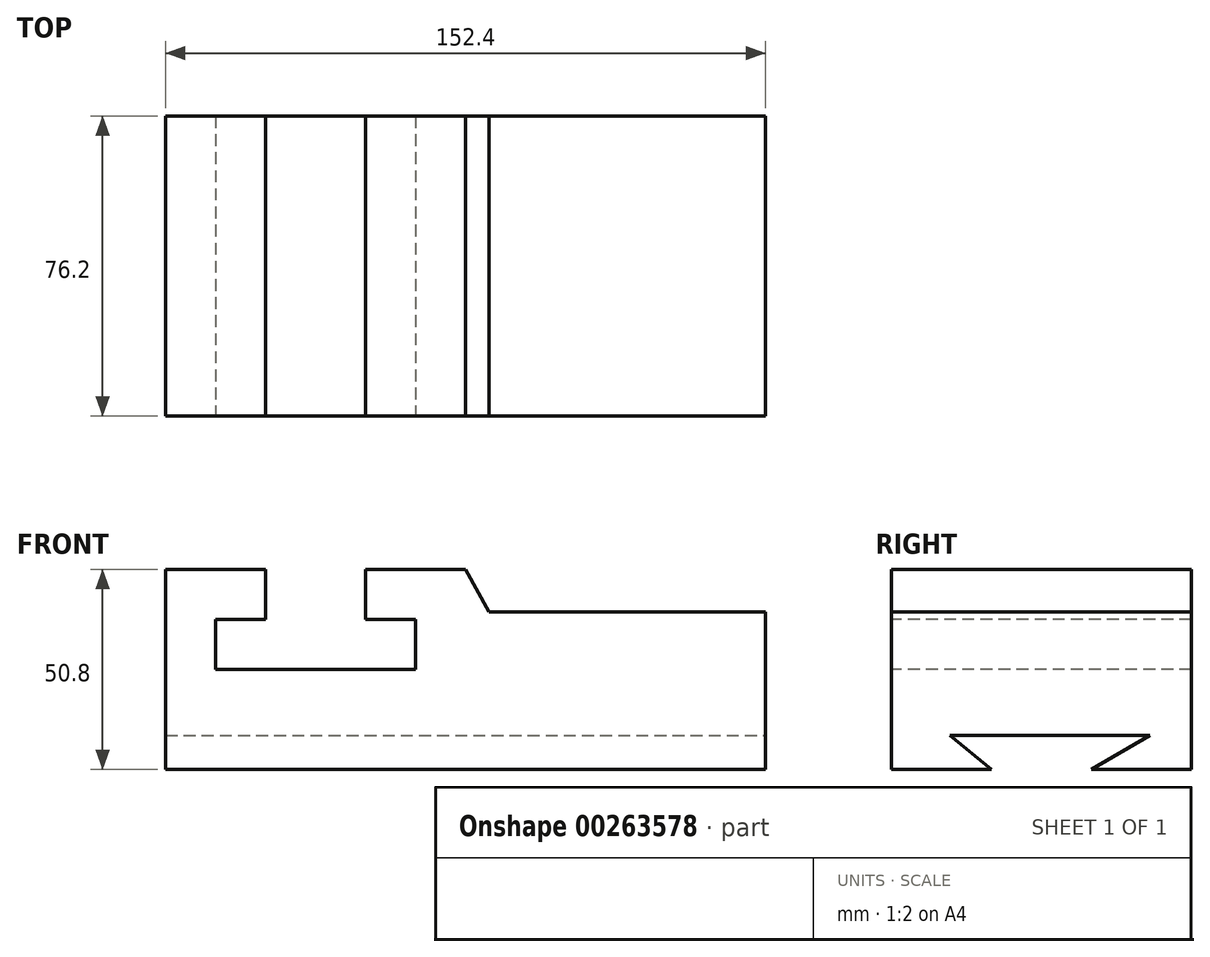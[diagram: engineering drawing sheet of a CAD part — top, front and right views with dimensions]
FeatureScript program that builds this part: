
annotation { "Feature Type Name" : "Feature", "Feature Type Description" : "" }
export const myFeature = defineFeature(function(context is Context, id is Id, definition is map)
    precondition{}
    {
        {
            var Q0;
            Q0=qCreatedBy(makeId("Front.planeOp"),FACE);
            var sketch = newSketch(context, id + "F0", { "sketchPlane" : qUnion([Q0])});
            skLineSegment(sketch, "E0.bottom", {"start": v(-122.18, 62.89) * mm, "end": v(30.22, 62.89) * mm});
            skLineSegment(sketch, "E0.top", {"start": v(-122.18, 12.09) * mm, "end": v(30.22, 12.09) * mm});
            skLineSegment(sketch, "E0.left", {"start": v(-122.18, 62.89) * mm, "end": v(-122.18, 12.09) * mm});
            skLineSegment(sketch, "E0.right", {"start": v(30.22, 62.89) * mm, "end": v(30.22, 12.09) * mm});
            skSolve(sketch);
        }
        {
            var Q0;
            Q0=makeQuery(id+"F0.imprint","IMPRINT",FACE,{"disambiguationData":[TD([[makeQuery(id+"F0.imprint","IMPRINT",EDGE,{"derivedFrom":sQuery(id+"F0.wireOp",EDGE,"E0.bottom")}),-1.0]])]});
            extrude(context, id + "F1", {"entities" : qUnion([Q0]), "depth" : 76.2 * mm});
        }
        {
            var Q0;
            Q0=makeQuery(id+"F1.opExtrude","CAP_FACE",FACE,{"disambiguationData":[OSD([sQuery(id+"F0.wireOp",EDGE,"E0.bottom"),sQuery(id+"F0.wireOp",EDGE,"E0.top"),sQuery(id+"F0.wireOp",EDGE,"E0.left"),sQuery(id+"F0.wireOp",EDGE,"E0.right")])],"isStart":false});
            var sketch = newSketch(context, id + "F2", { "sketchPlane" : qUnion([Q0])});
            skLineSegment(sketch, "E1", {"start": v(-96.78, 62.89) * mm, "end": v(-96.78, 50.19) * mm});
            skLineSegment(sketch, "E2", {"start": v(-96.78, 50.19) * mm, "end": v(-109.48, 50.19) * mm});
            skLineSegment(sketch, "E3", {"start": v(-109.48, 50.19) * mm, "end": v(-109.48, 37.49) * mm});
            skLineSegment(sketch, "E4", {"start": v(-109.48, 37.49) * mm, "end": v(-58.68, 37.49) * mm});
            skLineSegment(sketch, "E5", {"start": v(-58.68, 37.49) * mm, "end": v(-58.68, 50.19) * mm});
            skLineSegment(sketch, "E6", {"start": v(-58.68, 50.19) * mm, "end": v(-71.38, 50.19) * mm});
            skLineSegment(sketch, "E7", {"start": v(-71.38, 50.19) * mm, "end": v(-71.38, 62.89) * mm});
            skLineSegment(sketch, "E8", {"start": v(-71.38, 62.89) * mm, "end": v(-96.78, 62.89) * mm});
            skSolve(sketch);
        }
        {
            var Q0;
            Q0 = qSketchRegion(id + "F2", true);
            extrude(context, id + "F3", {"entities" : qUnion([Q0]), "operationType" : NewBodyOperationType.REMOVE, "endBound" : BoundingType.THROUGH_ALL, "oppositeDirection" : true, "depth" : 25.4 * mm});
        }
        {
            var Q0;
            Q0=makeQuery(id+"F1.opExtrude","CAP_FACE",FACE,{"disambiguationData":[OSD([sQuery(id+"F0.wireOp",EDGE,"E0.bottom"),sQuery(id+"F0.wireOp",EDGE,"E0.top"),sQuery(id+"F0.wireOp",EDGE,"E0.left"),sQuery(id+"F0.wireOp",EDGE,"E0.right")])],"isStart":false});
            var sketch = newSketch(context, id + "F4", { "sketchPlane" : qUnion([Q0])});
            skLineSegment(sketch, "E9", {"start": v(-71.38, 62.89) * mm, "end": v(-45.98, 62.89) * mm});
            skLineSegment(sketch, "E10", {"start": v(-45.98, 62.89) * mm, "end": v(-39.97, 52.1) * mm});
            skLineSegment(sketch, "E11", {"start": v(-39.97, 52.1) * mm, "end": v(30.22, 52.1) * mm});
            skLineSegment(sketch, "E12", {"start": v(30.22, 52.1) * mm, "end": v(30.22, 62.89) * mm});
            skLineSegment(sketch, "E13", {"start": v(30.22, 62.89) * mm, "end": v(-45.98, 62.89) * mm});
            skSolve(sketch);
        }
        {
            var Q0;
            Q0 = qSketchRegion(id + "F4", true);
            extrude(context, id + "F5", {"entities" : qUnion([Q0]), "operationType" : NewBodyOperationType.REMOVE, "endBound" : BoundingType.THROUGH_ALL, "oppositeDirection" : true, "depth" : 25.4 * mm});
        }
        {
            var Q0;
            Q0=makeQuery(id+"F1.opExtrude","SWEPT_FACE",FACE,{"disambiguationData":[OSD([sQuery(id+"F0.wireOp",EDGE,"E0.right")])]});
            var sketch = newSketch(context, id + "F6", { "sketchPlane" : qUnion([Q0])});
            skLineSegment(sketch, "E14", {"start": v(-76.2, 12.09) * mm, "end": v(-50.8, 12.09) * mm});
            skLineSegment(sketch, "E15", {"start": v(-50.8, 12.09) * mm, "end": v(-61.3, 20.72) * mm});
            skLineSegment(sketch, "E16", {"start": v(-61.3, 20.72) * mm, "end": v(-10.5, 20.72) * mm});
            skLineSegment(sketch, "E17", {"start": v(-10.5, 20.72) * mm, "end": v(-25.4, 12.09) * mm});
            skLineSegment(sketch, "E18", {"start": v(-25.4, 12.09) * mm, "end": v(0, 12.09) * mm});
            skLineSegment(sketch, "E19", {"start": v(-50.8, 12.09) * mm, "end": v(-25.4, 12.09) * mm});
            skSolve(sketch);
        }
        {
            var Q0;
            Q0 = qSketchRegion(id + "F6", true);
            extrude(context, id + "F7", {"entities" : qUnion([Q0]), "operationType" : NewBodyOperationType.REMOVE, "endBound" : BoundingType.THROUGH_ALL, "oppositeDirection" : true, "depth" : 25.4 * mm});
        }
    });
